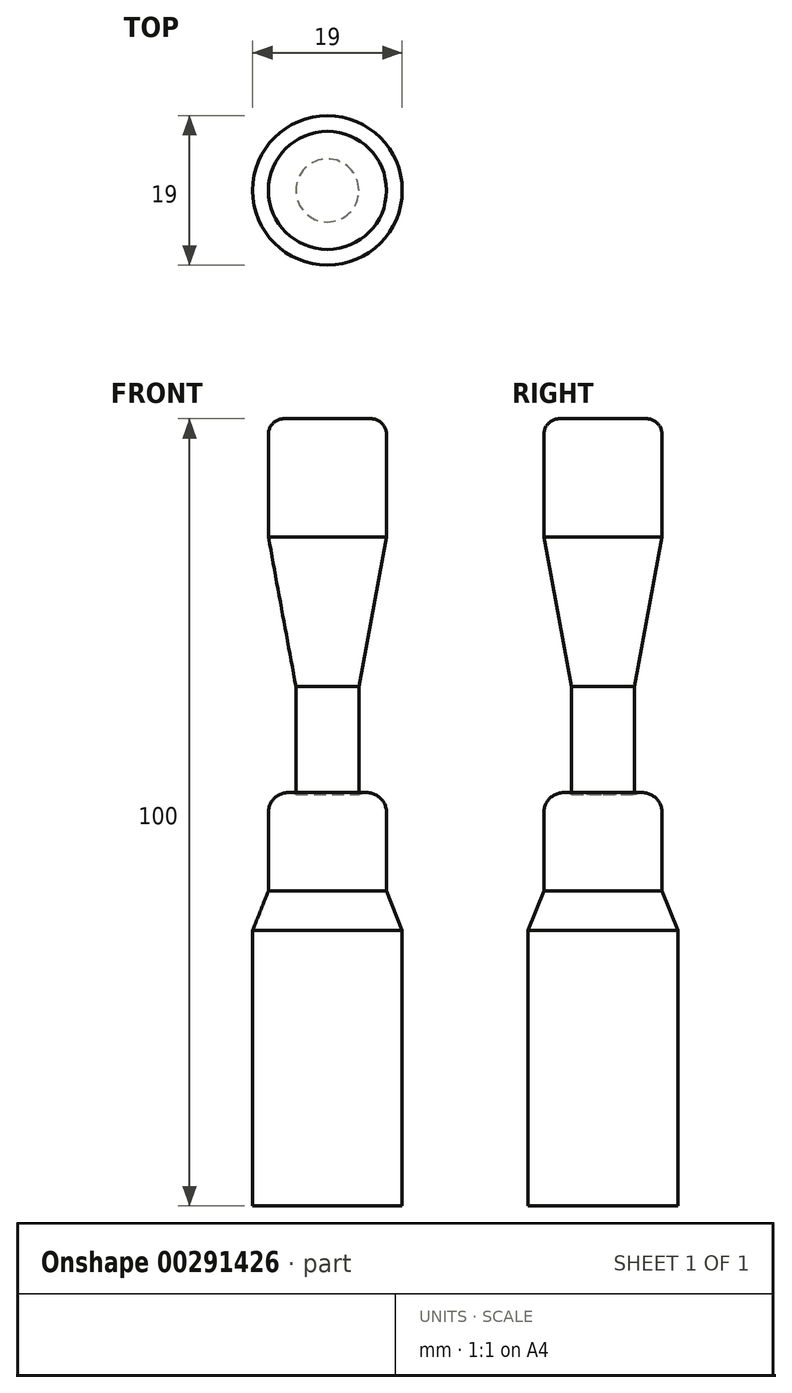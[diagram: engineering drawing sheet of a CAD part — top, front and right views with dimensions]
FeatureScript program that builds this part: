
annotation { "Feature Type Name" : "Feature", "Feature Type Description" : "" }
export const myFeature = defineFeature(function(context is Context, id is Id, definition is map)
    precondition{}
    {
        {
            var Q0;
            Q0=qCreatedBy(makeId("Front.planeOp"),FACE);
            var sketch = newSketch(context, id + "F0", { "sketchPlane" : qUnion([Q0])});
            skLineSegment(sketch, "E0", {"start": v(0, 0) * mm, "end": v(5.5, 0) * mm});
            skArc(sketch, "E1", {"start": v(7.5, -2) * mm, "mid": v(6.91, -0.59) * mm, "end": v(5.5, 0) * mm});
            skLineSegment(sketch, "E2", {"start": v(7.5, -2) * mm, "end": v(7.5, -15) * mm});
            skLineSegment(sketch, "E3", {"start": v(7.5, -15) * mm, "end": v(4, -34) * mm});
            skLineSegment(sketch, "E4", {"start": v(4, -34) * mm, "end": v(4, -47.7) * mm});
            skArc(sketch, "E5", {"start": v(7.5, -50) * mm, "mid": v(6.37, -47.9) * mm, "end": v(4, -47.7) * mm});
            skLineSegment(sketch, "E6", {"start": v(7.5, -50) * mm, "end": v(7.5, -60) * mm});
            skLineSegment(sketch, "E7", {"start": v(7.5, -60) * mm, "end": v(9.5, -65) * mm});
            skLineSegment(sketch, "E8", {"start": v(9.5, -65) * mm, "end": v(9.5, -100) * mm});
            skLineSegment(sketch, "E9", {"start": v(9.5, -100) * mm, "end": v(0, -100) * mm});
            skLineSegment(sketch, "E10", {"start": v(0, -100) * mm, "end": v(0, 0) * mm});
            skSolve(sketch);
        }
        {
            var Q0;
            Q0=makeQuery(id+"F0.imprint","IMPRINT",FACE,{"disambiguationData":[TD([[makeQuery(id+"F0.imprint","IMPRINT",EDGE,{"derivedFrom":sQuery(id+"F0.wireOp",EDGE,"E0")}),-1.0]])]});
            var Q1;
            Q1=sQuery(id+"F0.wireOp",EDGE,"E10");
            revolve(context, id + "F1", {"entities" : qUnion([Q0]), "axis" : qUnion([Q1]), "revolveType" : RevolveType.FULL});
        }
    });
